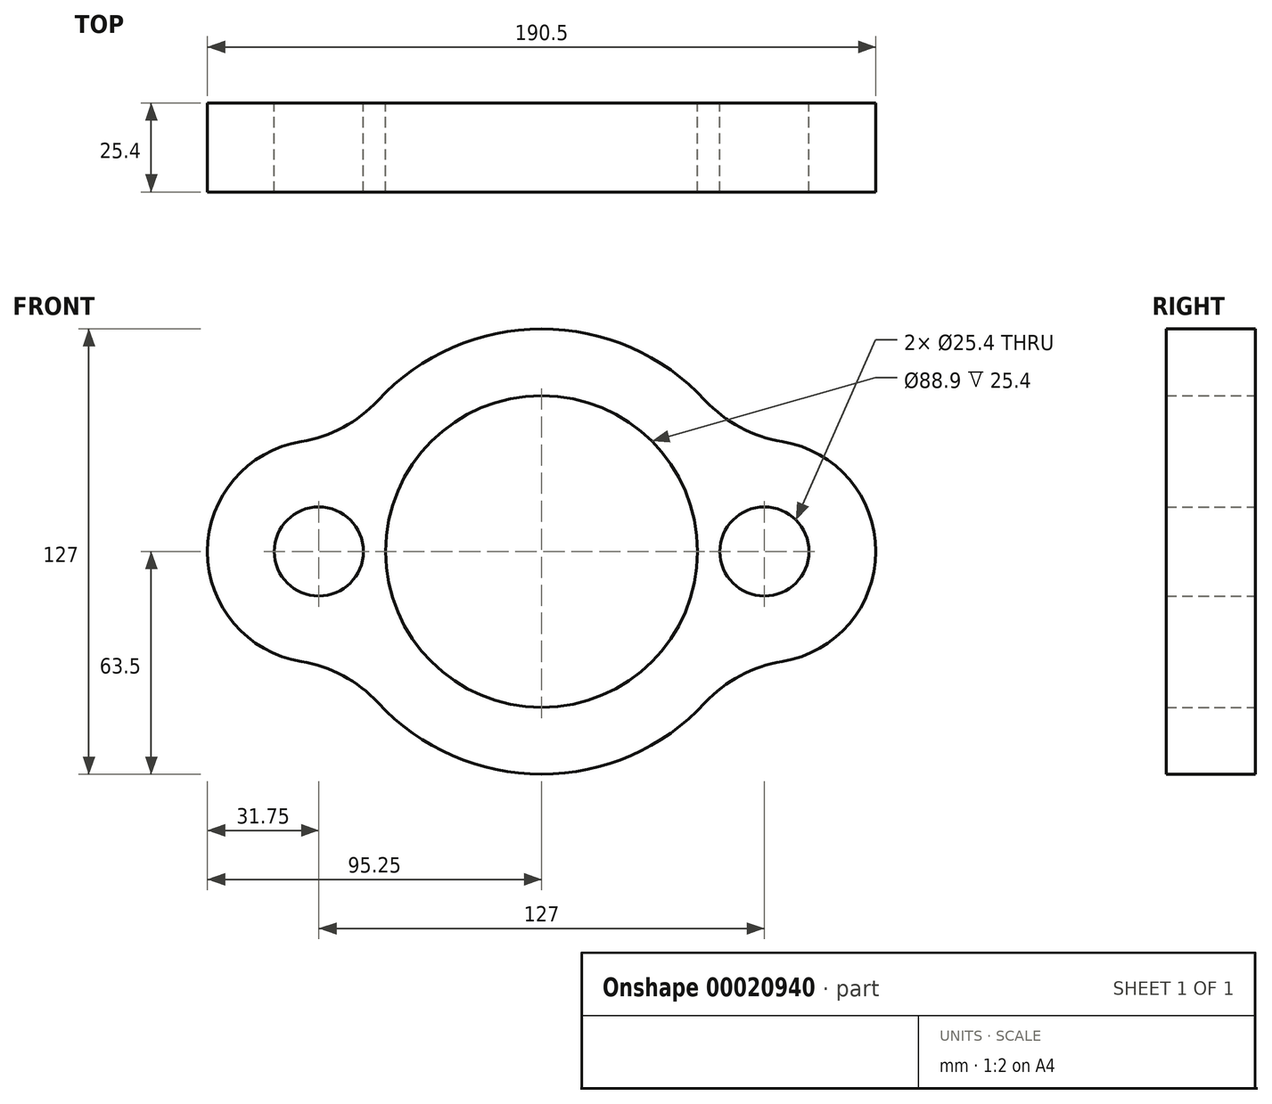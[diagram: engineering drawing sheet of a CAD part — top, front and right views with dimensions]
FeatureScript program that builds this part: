
annotation { "Feature Type Name" : "Feature", "Feature Type Description" : "" }
export const myFeature = defineFeature(function(context is Context, id is Id, definition is map)
    precondition{}
    {
        {
            var Q0;
            Q0=qCreatedBy(makeId("Front.planeOp"),FACE);
            var sketch = newSketch(context, id + "F0", { "sketchPlane" : qUnion([Q0])});
            skCircle(sketch, "E0", {"center": v(0, 0) * mm, "radius": 44.45 * mm});
            skArc(sketch, "E1", {"start": v(-46.63, -43.1) * mm, "mid": v(0, -63.5) * mm, "end": v(46.63, -43.1) * mm});
            skLineSegment(sketch, "E2", {"start": v(0, 0) * mm, "end": v(-3, 0) * mm});
            skLineSegment(sketch, "E3", {"start": v(3.06, 0) * mm, "end": v(-3, 0) * mm});
            skCircle(sketch, "E4", {"center": v(63.5, 0) * mm, "radius": 12.7 * mm});
            skCircle(sketch, "E5", {"center": v(-63.5, 0) * mm, "radius": 12.7 * mm});
            skArc(sketch, "E6", {"start": v(-68.55, 31.35) * mm, "mid": v(-95.25, 0) * mm, "end": v(-68.55, -31.35) * mm});
            skArc(sketch, "E7", {"start": v(68.55, -31.35) * mm, "mid": v(95.25, 0) * mm, "end": v(68.55, 31.35) * mm});
            skArc(sketch, "E8.trimOffspring", {"start": v(46.63, 43.1) * mm, "mid": v(0, 63.5) * mm, "end": v(-46.63, 43.1) * mm});
            skPoint(sketch, "E9.visualSharp", {"position": v(-55.56, 30.74) * mm});
            skArc(sketch, "E9.filletArc", {"start": v(-68.55, 31.35) * mm, "mid": v(-56.6, 35.38) * mm, "end": v(-46.63, 43.1) * mm});
            skPoint(sketch, "E10.visualSharp", {"position": v(55.56, 30.74) * mm});
            skArc(sketch, "E10.filletArc", {"start": v(46.63, 43.1) * mm, "mid": v(56.6, 35.38) * mm, "end": v(68.55, 31.35) * mm});
            skPoint(sketch, "E11.visualSharp", {"position": v(55.56, -30.74) * mm});
            skArc(sketch, "E11.filletArc", {"start": v(68.55, -31.35) * mm, "mid": v(56.6, -35.38) * mm, "end": v(46.63, -43.1) * mm});
            skPoint(sketch, "E12.visualSharp", {"position": v(-55.56, -30.74) * mm});
            skArc(sketch, "E12.filletArc", {"start": v(-46.63, -43.1) * mm, "mid": v(-56.6, -35.38) * mm, "end": v(-68.55, -31.35) * mm});
            skSolve(sketch);
        }
        {
            var Q0;
            Q0=makeQuery(id+"F0.imprint","IMPRINT",FACE,{"disambiguationData":[TD([[makeQuery(id+"F0.imprint","IMPRINT",EDGE,{"derivedFrom":sQuery(id+"F0.wireOp",EDGE,"E0")}),-1.0]])]});
            extrude(context, id + "F1", {"entities" : qUnion([Q0]), "depth" : 25.4 * mm});
        }
    });
